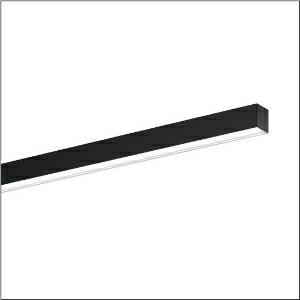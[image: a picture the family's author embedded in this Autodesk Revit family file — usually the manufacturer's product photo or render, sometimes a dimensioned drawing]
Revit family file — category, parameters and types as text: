
# Revit family: silica_21_51mx20da32bb
name_source: partatom
category: Lighting Fixtures
units: mm (PartAtom-declared; Revit-internal decimal feet)

## family parameters
Cut with Voids When Loaded = No
Host = Face
Light Source = No
Part Type = Normal
Room Calculation Point = No
Round Connector Dimension = Use Diameter
Shared = No

## types (1)
- --- (1 x LED, 2400 lm, 16.1 W, 3000K)
    Apparent Load = 16 VA
    CIE Flux Codes = 48 79 96 100 100
    Color Rendering = 80
    Color Temperature = 3000K
    Default Elevation = 1800 mm
    Description = Silica 21, office luminaire, primary optical cover: cover, of PMMA, opal, light emission: direct distribution, primary light characteristic: symmetric, installation type: surface-mounted, LED, rated luminous flux: 2.400lm, luminous efficacy: 149lm/W, light colour: 830, colour temperature: 3000K, control gear: DALI 2, with terminal, 3+2-pole, max. 2.5mm², mains connection: 220..240V, AC, 50/60Hz, rated input power: 16.1W, luminaire housing, of aluminium, matt jet black (RAL 9005), length: 1.204mm, width: 53mm, height: 53mm, protection rating (complete): IP20, insulation class (complete): insulation class I (protective earthing), certification: CE, permissible operating ambient temperature: 0..+35°C, standard: EN 50419, packaging unit: 1 piece
    Height = 53 mm
    Lamp = 1 x LED
    Lamp Light Flux = 2400 lm
    Lamp Power = 16.1 W
    Lamp count = 1
    Length = 1204 mm
    Luminous efficacy = 149 lm/W
    Manufacturer = Siteco
    ModVariant = No
    Model = 51MX20DA32BB
    Mounting Place = Ceiling
    Mounting Type = Surface mounted
    Number of Poles = 1
    OnlyDefault = Yes
    Power Factor = 1
    Product Name = Silica 21
    Product group = office luminaire | ceiling mounted
    ProductGroupID = 301
    Protection Class = Protection class I
    Protection Degree = IP 20
    RLX_Detail_Level = 1
    RLX_Emergency_Light_Flux = 0 lm
    RLX_Emergency_Type = 0
    RLX_Emergency_Type_DB = No
    RlxData = <blob elided: 28721 chars, md5=93574155>
    Socket = socket
    Standby Power = 0 W
    System Light Flux = 2400 lm
    System Power = 16 W
    Type Comments = factory setting: luminous flux: 100 % | dim-lin: 254 | 233 mA
    Type Image = l_1335925.jpg
    URL = http://relux.com
    VarID = @adj_027833
    Voltage = 0 V
    Weight = 0.00 kg
    Width = 53 mm

## geometry (parser evidence)
native form markers: Blend x4, Sweep x8
no freeform markers — native parametric forms only
